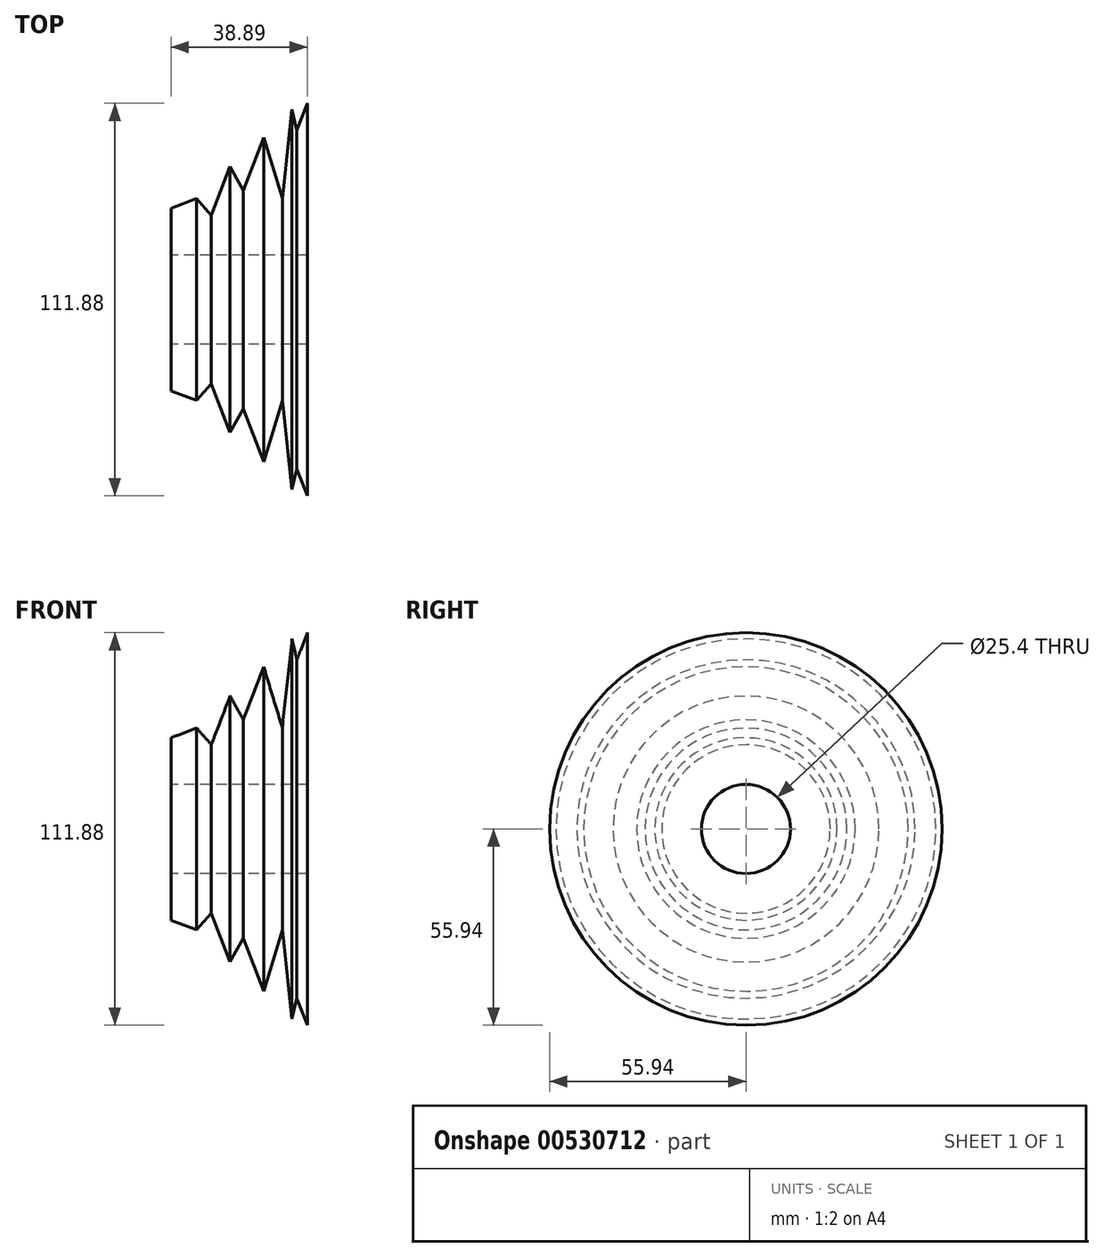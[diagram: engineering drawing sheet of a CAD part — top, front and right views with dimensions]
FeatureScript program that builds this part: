
annotation { "Feature Type Name" : "Feature", "Feature Type Description" : "" }
export const myFeature = defineFeature(function(context is Context, id is Id, definition is map)
    precondition{}
    {
        {
            var Q0;
            Q0=qCreatedBy(makeId("Front.planeOp"),FACE);
            var sketch = newSketch(context, id + "F0", { "sketchPlane" : qUnion([Q0])});
            skLineSegment(sketch, "E0", {"start": v(0, 0) * mm, "end": v(-95.65, 0) * mm});
            skLineSegment(sketch, "E1", {"start": v(0, 12.7) * mm, "end": v(-38.7, 12.7) * mm});
            skLineSegment(sketch, "E2", {"start": v(-38.7, 12.7) * mm, "end": v(-38.7, 26) * mm});
            skLineSegment(sketch, "E3", {"start": v(-38.9, 26) * mm, "end": v(-31.55, 28.77) * mm});
            skLineSegment(sketch, "E4", {"start": v(-31.55, 28.77) * mm, "end": v(-27.38, 24.01) * mm});
            skLineSegment(sketch, "E5", {"start": v(-27.38, 24.01) * mm, "end": v(-22.03, 37.9) * mm});
            skLineSegment(sketch, "E6", {"start": v(-22.03, 37.9) * mm, "end": v(-18.26, 31.15) * mm});
            skLineSegment(sketch, "E7", {"start": v(-18.26, 31.15) * mm, "end": v(-12.43, 46.25) * mm});
            skLineSegment(sketch, "E8", {"start": v(-12.43, 46.25) * mm, "end": v(-7.14, 28.77) * mm});
            skLineSegment(sketch, "E9", {"start": v(-7.14, 28.77) * mm, "end": v(-4.37, 54.17) * mm});
            skLineSegment(sketch, "E10", {"start": v(-4.37, 54.17) * mm, "end": v(-2.98, 48.22) * mm});
            skLineSegment(sketch, "E11", {"start": v(-2.98, 48.22) * mm, "end": v(0, 55.94) * mm});
            skLineSegment(sketch, "E12", {"start": v(0, 55.94) * mm, "end": v(0, 12.7) * mm});
            skSolve(sketch);
        }
        {
            var Q0;
            Q0=sQuery(id+"F0.wireOp",EDGE,"E8");
            var Q1;
            Q1=sQuery(id+"F0.wireOp",EDGE,"E6");
            var Q2;
            Q2=sQuery(id+"F0.wireOp",EDGE,"E7");
            var Q3;
            Q3=sQuery(id+"F0.wireOp",EDGE,"E4");
            var Q4;
            Q4=sQuery(id+"F0.wireOp",EDGE,"E5");
            var Q5;
            Q5=sQuery(id+"F0.wireOp",EDGE,"E3");
            var Q6;
            Q6=sQuery(id+"F0.wireOp",EDGE,"E1");
            var Q7;
            Q7=sQuery(id+"F0.wireOp",EDGE,"E2");
            var Q8;
            Q8=sQuery(id+"F0.wireOp",EDGE,"E9");
            var Q9;
            Q9=sQuery(id+"F0.wireOp",EDGE,"E10");
            var Q10;
            Q10=sQuery(id+"F0.wireOp",EDGE,"E11");
            var Q11;
            Q11=sQuery(id+"F0.wireOp",EDGE,"E12");
            var Q12;
            Q12=sQuery(id+"F0.wireOp",EDGE,"E0");
            revolve(context, id + "F1", {"bodyType" : ToolBodyType.SURFACE, "surfaceEntities" : qUnion([Q0, Q1, Q2, Q3, Q4, Q5, Q6, Q7, Q8, Q9, Q10, Q11]), "axis" : qUnion([Q12]), "revolveType" : RevolveType.FULL});
        }
    });
